# Revit family: Gym Lighting-High_Bay-Philips_Day-Brite-HB-FGL-4Lamp
name_source: partatom
category: Lighting Fixtures
revit_build: Autodesk Revit Architecture 2012 (Build: 20110309_2315(x64)
units: mm (PartAtom-declared; Revit-internal decimal feet)

## types (5) — shared parameters
Assembly Code = D5020200
Bare Lamp = Default Light Source
CIE Type = Direct
Color Filter = 16777215
Default Elevation = 48"
Depth = 2 3/4"
Dimming Lamp Color Temperature Shift = <None>
Emit Shape Visible in Rendering = No
Emit from Rectangle Length = 49 1/2"
Emit from Rectangle Width = 13 3/8"
Housing Material Finish = Paint-Philips Day-Brite-White
Lamp Position = Horizontal
Length = 49 1/2"
Manufacturer = Philips Day-Brite
NEMA Type = Not Applicable
Number of Lamps or LEDs = 4
Options = White Wire Guard
Product Family = FGL Fluorescent Gymnasium Luminaire
Product Page URL = http://www.daybrite.com
Reflector Material Finish = Aluminum-Philips Day-Brite-MIRO4
Reflector Option = Miro4 Contoured Reflector
Spacing to Mounting Height Ratio 0 Degree Plane = 1.26
Specification Sheet = HB-10034
Tilt Angle = -90.00°
URL = http://www.daybrite.com
Width = 17"

## per-type parameters (varying)
| type | Apparent Load | Description | Fixture Efficiency | LER Luminaire Efficacy Rating | Lamp | Photometric Web File | Spacing to Mounting Height Ratio 90 Degree Plane | Spacing to Mounting Height Ratio Diagonal | Voltage | Voltage Comments |
| FGL432-120-MC-1/4-EB-WG | 112 VA | FGL Fluorescent Gym Luminaire w/Wire Guard, (4)F32T8 Lamps | 83.5% | 90 | F32T8 | 27384.IES | 1.04 | 1.24 | 120 V | 120 |
| FGL432-277-MC-1/4-EB-WG | 112 VA | FGL Fluorescent Gym Luminaire w/Wire Guard, (4)F32T8 Lamps | 83.5% | 90 | F32T8 | 27384.IES | 1.04 | 1.24 | 277 V | 277 |
| FGL454HO-120-MC-1/4-EB-WG | 240 VA | FGL Fluorescent Gym Luminaire w/Wire Guard, (4)F54T5HO Lamps | 86.2% | 65 | F54T5HO | 25625.IES | 0.8 | 1.04 | 120 V | 120 |
| FGL454HO-277-MC-1/4-EB-WG | 240 VA | FGL Fluorescent Gym Luminaire w/Wire Guard, (4)F54T5HO Lamps | 86.2% | 65 | F54T5HO | 25625.IES | 0.8 | 1.04 | 277 V | 277 |
| FGL454HO-480-MC-1/4-EB-WG | 239 VA | FGL Fluorescent Gym Luminaire w/Wire Guard, (4)F54T5HO Lamps | 86.2% | 65 | F54T5HO | 25625.IES | 0.8 | 1.04 | 480 V | 480 |

note: column(s) folded — value = type name in every type: Catalog Number, Model

## geometry (parser evidence)
native form markers: Blend x2, Sweep x1
no freeform markers — native parametric forms only
